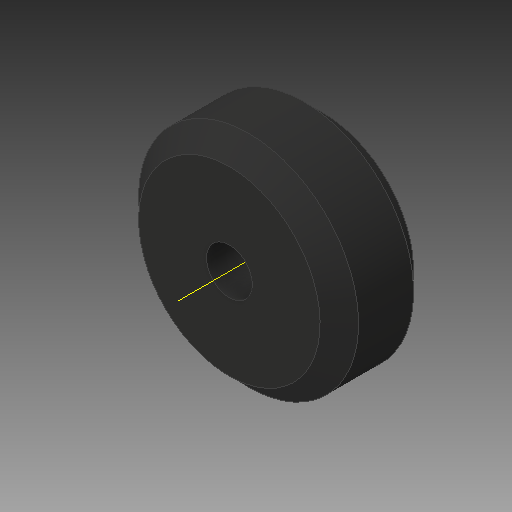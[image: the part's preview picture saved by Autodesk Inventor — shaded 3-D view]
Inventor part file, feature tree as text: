
AUTODESK INVENTOR PART (.ipt)
format: ipt  version: 2019 (Build 230136000, 136)  size: 104,448 bytes
history: native  units: in
note: dims shown in document units (in); Inventor stores cm internally (conversion verified against a paired STEP export)
features: revolve x1, other x1, sketch x1
ambient origin geometry x8: Origin, YZ Plane, XZ Plane, XY Plane, X Axis, Y Axis, Z Axis, Center Point
bodies: Solid1 (feature_tree)
feature tree (3):
  revolve  "Revolution1"  [1 undecoded]
  other  "Work Axis1"
  sketch  "Sketch2"  dims[d5=0.2362in d8=0.4016in d11=90.0deg]
note: 1 required parameter value undecoded (feature->parameter linkage not recoverable at this tier; creation-order binding heuristic only, values carry confidence <= 0.55)
